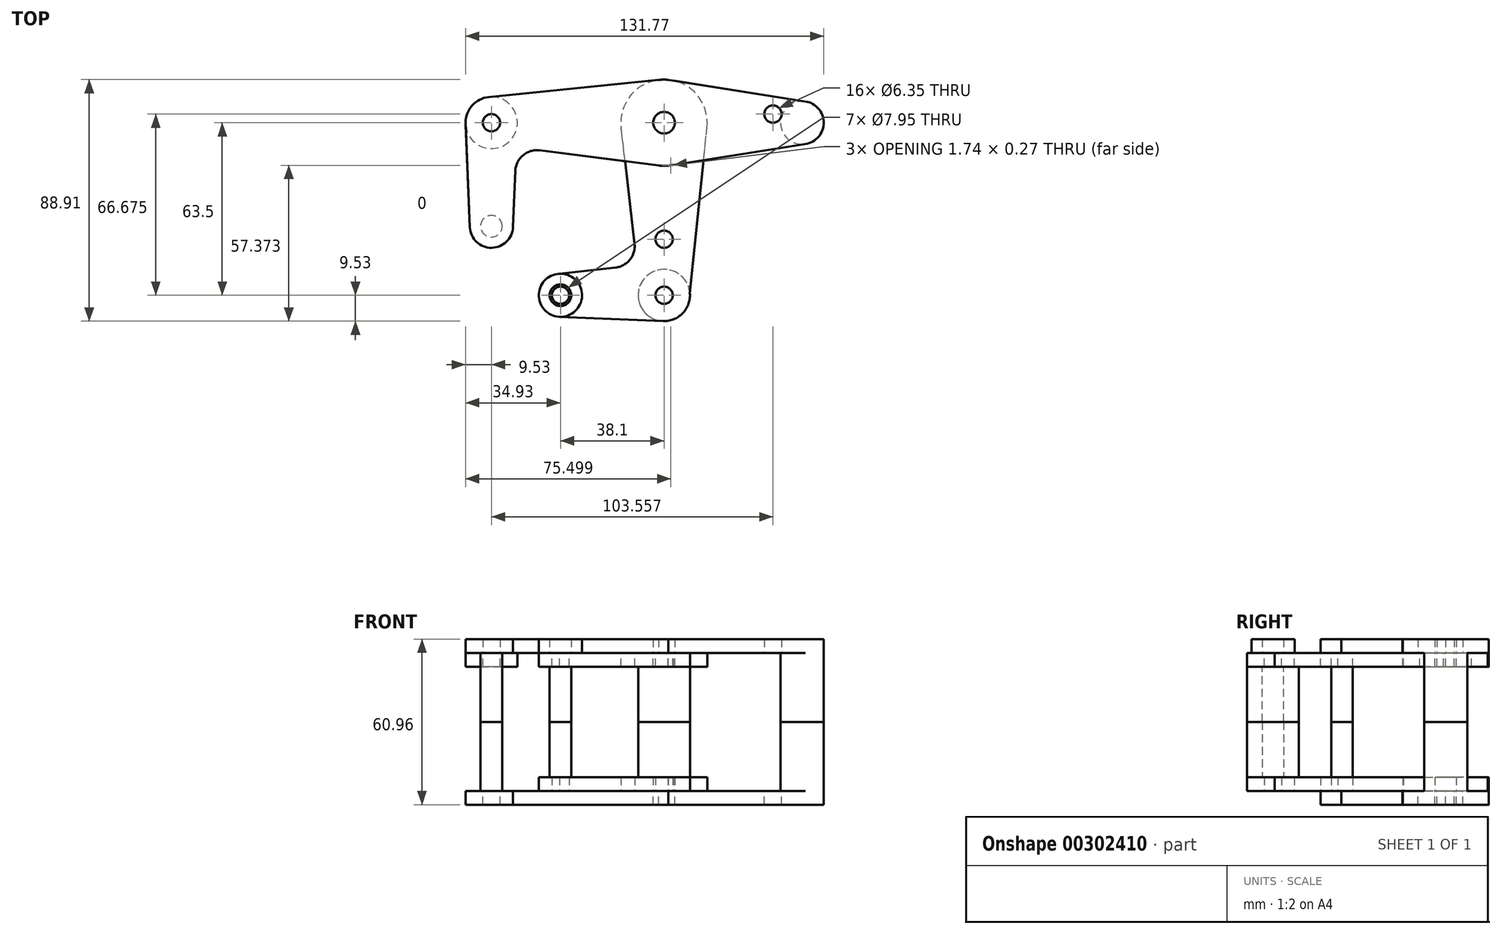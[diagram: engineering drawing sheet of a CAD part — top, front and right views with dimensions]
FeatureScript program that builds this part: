
annotation { "Feature Type Name" : "Feature", "Feature Type Description" : "" }
export const myFeature = defineFeature(function(context is Context, id is Id, definition is map)
    precondition{}
    {
        {
            var Q0;
            Q0=qCreatedBy(makeId("Top.planeOp"),FACE);
            var sketch = newSketch(context, id + "F0", { "sketchPlane" : qUnion([Q0])});
            skCircle(sketch, "E0", {"center": v(0, 0) * mm, "radius": 15.88 * mm});
            skCircle(sketch, "E1", {"center": v(0, 0) * mm, "radius": 3.98 * mm});
            skLineSegment(sketch, "E2", {"start": v(0, 0) * mm, "end": v(50.8, 0) * mm, "construction": true});
            skCircle(sketch, "E3", {"center": v(50.8, 0) * mm, "radius": 7.94 * mm});
            skCircle(sketch, "E4", {"center": v(50.8, 0) * mm, "radius": 3.18 * mm});
            skLineSegment(sketch, "E5", {"start": v(0, 0) * mm, "end": v(-63.5, 0) * mm, "construction": true});
            skCircle(sketch, "E6", {"center": v(-63.5, 0) * mm, "radius": 9.53 * mm});
            skCircle(sketch, "E7", {"center": v(-63.5, 0) * mm, "radius": 3.18 * mm});
            skLineSegment(sketch, "E8", {"start": v(-63.5, 0) * mm, "end": v(-63.5, -38.1) * mm, "construction": true});
            skCircle(sketch, "E9", {"center": v(-63.5, -38.1) * mm, "radius": 7.94 * mm});
            skCircle(sketch, "E10", {"center": v(-63.5, -38.1) * mm, "radius": 3.18 * mm});
            skLineSegment(sketch, "E11", {"start": v(0, 0) * mm, "end": v(0, -63.5) * mm, "construction": true});
            skCircle(sketch, "E12", {"center": v(0, -63.5) * mm, "radius": 9.53 * mm});
            skCircle(sketch, "E13", {"center": v(0, -63.5) * mm, "radius": 3.18 * mm});
            skLineSegment(sketch, "E14", {"start": v(0, -63.5) * mm, "end": v(-38.1, -63.5) * mm, "construction": true});
            skCircle(sketch, "E15", {"center": v(-38.1, -63.5) * mm, "radius": 7.94 * mm});
            skCircle(sketch, "E16", {"center": v(-38.1, -63.5) * mm, "radius": 3.18 * mm});
            skCircle(sketch, "E17", {"center": v(0, -42.85) * mm, "radius": 3.18 * mm});
            skLineSegment(sketch, "E18", {"start": v(-55.57, -38.32) * mm, "end": v(-54.7, -17.73) * mm});
            skLineSegment(sketch, "E19", {"start": v(-45.76, -10.17) * mm, "end": v(-2, -15.75) * mm});
            skPoint(sketch, "E20.visualSharp", {"position": v(-54.35, -9.08) * mm});
            skArc(sketch, "E20.filletArc", {"start": v(-45.76, -10.17) * mm, "mid": v(-51.9, -11.98) * mm, "end": v(-54.7, -17.73) * mm});
            skLineSegment(sketch, "E21", {"start": v(-38.48, -55.57) * mm, "end": v(-17.9, -53.31) * mm});
            skLineSegment(sketch, "E22", {"start": v(-10.86, -44.5) * mm, "end": v(-15.77, -1.81) * mm});
            skPoint(sketch, "E23.visualSharp", {"position": v(-9.95, -52.44) * mm});
            skArc(sketch, "E23.filletArc", {"start": v(-17.9, -53.31) * mm, "mid": v(-12.54, -50.37) * mm, "end": v(-10.86, -44.5) * mm});
            skLineSegment(sketch, "E24", {"start": v(-38.49, -71.43) * mm, "end": v(0, -73.03) * mm});
            skLineSegment(sketch, "E25", {"start": v(9.5, -62.84) * mm, "end": v(15.8, -1.62) * mm});
            skLineSegment(sketch, "E26", {"start": v(1.6, -15.8) * mm, "end": v(52.04, -7.84) * mm});
            skLineSegment(sketch, "E27", {"start": v(1.46, 15.8) * mm, "end": v(52.04, 7.84) * mm});
            skLineSegment(sketch, "E28", {"start": v(-1.98, 15.75) * mm, "end": v(-64.45, 9.48) * mm});
            skLineSegment(sketch, "E29", {"start": v(-73.03, 0) * mm, "end": v(-71.43, -38.43) * mm});
            skCircle(sketch, "E30", {"center": v(40.06, 3.18) * mm, "radius": 3.18 * mm});
            skCircle(sketch, "E31", {"center": v(-63.5, -38.1) * mm, "radius": 3.98 * mm});
            skCircle(sketch, "E32", {"center": v(-38.1, -63.5) * mm, "radius": 3.98 * mm});
            skSolve(sketch);
        }
        {
            var Q0;
            {var subQ0=sQuery(id+"F0.wireOp",EDGE,"E27");var subQ1=sQuery(id+"F0.wireOp",EDGE,"E0");var subQ2=makeQuery(id+"F0.imprint","INTERSECT",VERTEX,{"disambiguationData":[OD(0.0)],"derivedFrom":[subQ1,subQ0]});Q0=makeQuery(id+"F0.imprint","IMPRINT",FACE,{"disambiguationData":[TD([[makeQuery(id+"F0.imprint","IMPRINT",EDGE,{"disambiguationData":[TD([[subQ2,1.0]])],"derivedFrom":subQ1}),1.0]])]});}
            var Q1;
            {var subQ0=sQuery(id+"F0.wireOp",EDGE,"E29");var subQ1=sQuery(id+"F0.wireOp",EDGE,"E6");var subQ2=makeQuery(id+"F0.imprint","INTERSECT",VERTEX,{"disambiguationData":[OD(0.0)],"derivedFrom":[subQ1,subQ0]});Q1=makeQuery(id+"F0.imprint","IMPRINT",FACE,{"disambiguationData":[TD([[makeQuery(id+"F0.imprint","IMPRINT",EDGE,{"disambiguationData":[TD([[subQ2,-1.0]])],"derivedFrom":subQ1}),1.0]])]});}
            var Q2;
            {var subQ0=sQuery(id+"F0.wireOp",EDGE,"E24");var subQ1=sQuery(id+"F0.wireOp",EDGE,"E15");var subQ2=makeQuery(id+"F0.imprint","INTERSECT",VERTEX,{"disambiguationData":[OD(0.0)],"derivedFrom":[subQ1,subQ0]});Q2=makeQuery(id+"F0.imprint","IMPRINT",FACE,{"disambiguationData":[TD([[makeQuery(id+"F0.imprint","IMPRINT",EDGE,{"disambiguationData":[TD([[subQ2,-1.0]])],"derivedFrom":subQ1}),1.0]])]});}
            var Q3;
            Q3=makeQuery(id+"F0.imprint","IMPRINT",FACE,{"disambiguationData":[TD([[makeQuery(id+"F0.imprint","IMPRINT",EDGE,{"derivedFrom":sQuery(id+"F0.wireOp",EDGE,"E4")}),-1.0]])]});
            var Q4;
            Q4=makeQuery(id+"F0.imprint","IMPRINT",FACE,{"disambiguationData":[TD([[makeQuery(id+"F0.imprint","IMPRINT",EDGE,{"derivedFrom":sQuery(id+"F0.wireOp",EDGE,"E10")}),-1.0]])]});
            var Q5;
            {var subQ0=sQuery(id+"F0.wireOp",EDGE,"E19");var subQ1=sQuery(id+"F0.wireOp",EDGE,"E0");var subQ2=makeQuery(id+"F0.imprint","INTERSECT",VERTEX,{"derivedFrom":[subQ1,subQ0]});Q5=makeQuery(id+"F0.imprint","IMPRINT",FACE,{"disambiguationData":[TD([[makeQuery(id+"F0.imprint","IMPRINT",EDGE,{"disambiguationData":[TD([[subQ2,1.0]])],"derivedFrom":subQ1}),-1.0]])]});}
            var Q6;
            {var subQ0=sQuery(id+"F0.wireOp",EDGE,"E25");var subQ1=sQuery(id+"F0.wireOp",EDGE,"E0");var subQ2=makeQuery(id+"F0.imprint","INTERSECT",VERTEX,{"derivedFrom":[subQ1,subQ0]});Q6=makeQuery(id+"F0.imprint","IMPRINT",FACE,{"disambiguationData":[TD([[makeQuery(id+"F0.imprint","IMPRINT",EDGE,{"disambiguationData":[TD([[subQ2,1.0]])],"derivedFrom":subQ1}),-1.0]])]});}
            var Q7;
            Q7=makeQuery(id+"F0.imprint","IMPRINT",FACE,{"disambiguationData":[TD([[makeQuery(id+"F0.imprint","IMPRINT",EDGE,{"derivedFrom":sQuery(id+"F0.wireOp",EDGE,"E7")}),-1.0]])]});
            var Q8;
            {var subQ4=sQuery(id+"F0.wireOp",EDGE,"E18");Q8=makeQuery(id+"F0.imprint","IMPRINT",FACE,{"disambiguationData":[TD([[makeQuery(id+"F0.imprint","IMPRINT",EDGE,{"derivedFrom":subQ4}),1.0]])]});}
            var Q9;
            Q9=makeQuery(id+"F0.imprint","IMPRINT",FACE,{"disambiguationData":[TD([[makeQuery(id+"F0.imprint","IMPRINT",EDGE,{"derivedFrom":sQuery(id+"F0.wireOp",EDGE,"E30")}),-1.0]])]});
            var Q10;
            Q10=makeQuery(id+"F0.imprint","IMPRINT",FACE,{"disambiguationData":[TD([[makeQuery(id+"F0.imprint","IMPRINT",EDGE,{"derivedFrom":sQuery(id+"F0.wireOp",EDGE,"E1")}),-1.0]])]});
            var Q11;
            Q11=makeQuery(id+"F0.imprint","IMPRINT",FACE,{"disambiguationData":[TD([[makeQuery(id+"F0.imprint","IMPRINT",EDGE,{"derivedFrom":sQuery(id+"F0.wireOp",EDGE,"E31")}),-1.0]])]});
            extrude(context, id + "F1", {"entities" : qUnion([Q0, Q1, Q2, Q3, Q4, Q5, Q6, Q7, Q8, Q9, Q10, Q11]), "depth" : 5.08 * mm});
        }
        {
            var Q0;
            {var subQ0=sQuery(id+"F0.wireOp",EDGE,"E27");var subQ1=sQuery(id+"F0.wireOp",EDGE,"E0");var subQ2=makeQuery(id+"F0.imprint","INTERSECT",VERTEX,{"disambiguationData":[OD(0.0)],"derivedFrom":[subQ1,subQ0]});Q0=makeQuery(id+"F0.imprint","IMPRINT",FACE,{"disambiguationData":[TD([[makeQuery(id+"F0.imprint","IMPRINT",EDGE,{"disambiguationData":[TD([[subQ2,1.0]])],"derivedFrom":subQ1}),1.0]])]});}
            var Q1;
            {var subQ0=sQuery(id+"F0.wireOp",EDGE,"E29");var subQ1=sQuery(id+"F0.wireOp",EDGE,"E6");var subQ2=makeQuery(id+"F0.imprint","INTERSECT",VERTEX,{"disambiguationData":[OD(0.0)],"derivedFrom":[subQ1,subQ0]});Q1=makeQuery(id+"F0.imprint","IMPRINT",FACE,{"disambiguationData":[TD([[makeQuery(id+"F0.imprint","IMPRINT",EDGE,{"disambiguationData":[TD([[subQ2,-1.0]])],"derivedFrom":subQ1}),1.0]])]});}
            var Q2;
            {var subQ0=sQuery(id+"F0.wireOp",EDGE,"E24");var subQ1=sQuery(id+"F0.wireOp",EDGE,"E15");var subQ2=makeQuery(id+"F0.imprint","INTERSECT",VERTEX,{"disambiguationData":[OD(0.0)],"derivedFrom":[subQ1,subQ0]});Q2=makeQuery(id+"F0.imprint","IMPRINT",FACE,{"disambiguationData":[TD([[makeQuery(id+"F0.imprint","IMPRINT",EDGE,{"disambiguationData":[TD([[subQ2,-1.0]])],"derivedFrom":subQ1}),1.0]])]});}
            var Q3;
            Q3=makeQuery(id+"F0.imprint","IMPRINT",FACE,{"disambiguationData":[TD([[makeQuery(id+"F0.imprint","IMPRINT",EDGE,{"derivedFrom":sQuery(id+"F0.wireOp",EDGE,"E13")}),-1.0]])]});
            var Q4;
            {var subQ0=sQuery(id+"F0.wireOp",EDGE,"E19");var subQ1=sQuery(id+"F0.wireOp",EDGE,"E0");var subQ2=makeQuery(id+"F0.imprint","INTERSECT",VERTEX,{"derivedFrom":[subQ1,subQ0]});Q4=makeQuery(id+"F0.imprint","IMPRINT",FACE,{"disambiguationData":[TD([[makeQuery(id+"F0.imprint","IMPRINT",EDGE,{"disambiguationData":[TD([[subQ2,1.0]])],"derivedFrom":subQ1}),-1.0]])]});}
            var Q5;
            {var subQ0=sQuery(id+"F0.wireOp",EDGE,"E25");var subQ1=sQuery(id+"F0.wireOp",EDGE,"E0");var subQ2=makeQuery(id+"F0.imprint","INTERSECT",VERTEX,{"derivedFrom":[subQ1,subQ0]});Q5=makeQuery(id+"F0.imprint","IMPRINT",FACE,{"disambiguationData":[TD([[makeQuery(id+"F0.imprint","IMPRINT",EDGE,{"disambiguationData":[TD([[subQ2,1.0]])],"derivedFrom":subQ1}),-1.0]])]});}
            var Q6;
            Q6=makeQuery(id+"F0.imprint","IMPRINT",FACE,{"disambiguationData":[TD([[makeQuery(id+"F0.imprint","IMPRINT",EDGE,{"derivedFrom":sQuery(id+"F0.wireOp",EDGE,"E17")}),-1.0]])]});
            var Q7;
            Q7=makeQuery(id+"F0.imprint","IMPRINT",FACE,{"disambiguationData":[TD([[makeQuery(id+"F0.imprint","IMPRINT",EDGE,{"derivedFrom":sQuery(id+"F0.wireOp",EDGE,"E1")}),-1.0]])]});
            var Q8;
            Q8=makeQuery(id+"F0.imprint","IMPRINT",FACE,{"disambiguationData":[TD([[makeQuery(id+"F0.imprint","IMPRINT",EDGE,{"derivedFrom":sQuery(id+"F0.wireOp",EDGE,"E16")}),-1.0]])]});
            var Q9;
            Q9=makeQuery(id+"F0.imprint","IMPRINT",FACE,{"disambiguationData":[TD([[makeQuery(id+"F0.imprint","IMPRINT",EDGE,{"derivedFrom":sQuery(id+"F0.wireOp",EDGE,"E32")}),-1.0]])]});
            extrude(context, id + "F2", {"entities" : qUnion([Q0, Q1, Q2, Q3, Q4, Q5, Q6, Q7, Q8, Q9]), "oppositeDirection" : true, "depth" : 5.08 * mm});
        }
        {
            var Q0;
            Q0=qCreatedBy(makeId("Top.planeOp"),FACE);
            cPlane(context, id + "F3", {"entities" : qUnion([Q0]), "cplaneType" : CPlaneType.OFFSET, "offset" : 25.4 * mm, "oppositeDirection" : true, "width" : 152.4 * mm, "height" : 152.4 * mm});
        }
        {
            var Q0;
            Q0=makeQuery(id+"F0.imprint","IMPRINT",FACE,{"disambiguationData":[TD([[makeQuery(id+"F0.imprint","IMPRINT",EDGE,{"derivedFrom":sQuery(id+"F0.wireOp",EDGE,"E10")}),-1.0]])]});
            var Q1;
            Q1=makeQuery(id+"F0.imprint","IMPRINT",FACE,{"disambiguationData":[TD([[makeQuery(id+"F0.imprint","IMPRINT",EDGE,{"derivedFrom":sQuery(id+"F0.wireOp",EDGE,"E4")}),-1.0]])]});
            var Q2;
            Q2=makeQuery(id+"F0.imprint","IMPRINT",FACE,{"disambiguationData":[TD([[makeQuery(id+"F0.imprint","IMPRINT",EDGE,{"derivedFrom":sQuery(id+"F0.wireOp",EDGE,"E16")}),-1.0]])]});
            var Q3;
            Q3=makeQuery(id+"F0.imprint","IMPRINT",FACE,{"disambiguationData":[TD([[makeQuery(id+"F0.imprint","IMPRINT",EDGE,{"derivedFrom":sQuery(id+"F0.wireOp",EDGE,"E13")}),-1.0]])]});
            var Q4;
            Q4=makeQuery(id+"F0.imprint","IMPRINT",FACE,{"disambiguationData":[TD([[makeQuery(id+"F0.imprint","IMPRINT",EDGE,{"derivedFrom":sQuery(id+"F0.wireOp",EDGE,"E10")}),1.0]])]});
            var Q5;
            Q5=makeQuery(id+"F0.imprint","IMPRINT",FACE,{"disambiguationData":[TD([[makeQuery(id+"F0.imprint","IMPRINT",EDGE,{"derivedFrom":sQuery(id+"F0.wireOp",EDGE,"E16")}),1.0]])]});
            var Q6;
            Q6=makeQuery(id+"F0.imprint","IMPRINT",FACE,{"disambiguationData":[TD([[makeQuery(id+"F0.imprint","IMPRINT",EDGE,{"derivedFrom":sQuery(id+"F0.wireOp",EDGE,"E13")}),1.0]])]});
            var Q7;
            Q7=makeQuery(id+"F0.imprint","IMPRINT",FACE,{"disambiguationData":[TD([[makeQuery(id+"F0.imprint","IMPRINT",EDGE,{"derivedFrom":sQuery(id+"F0.wireOp",EDGE,"E4")}),1.0]])]});
            var Q8;
            Q8=qCreatedBy(id+"F3.planeOp",FACE);
            extrude(context, id + "F4", {"entities" : qUnion([Q0, Q1, Q2, Q3, Q4, Q5, Q6, Q7]), "endBound" : BoundingType.UP_TO_SURFACE, "oppositeDirection" : true, "endBoundEntityFace" : qUnion([Q8]), "depth" : 25.4 * mm});
        }
        {
            var Q0;
            Q0=makeQuery(id+"F0.imprint","IMPRINT",FACE,{"disambiguationData":[TD([[makeQuery(id+"F0.imprint","IMPRINT",EDGE,{"derivedFrom":sQuery(id+"F0.wireOp",EDGE,"E4")}),1.0]])]});
            extrude(context, id + "F5", {"entities" : qUnion([Q0]), "operationType" : NewBodyOperationType.ADD, "depth" : 5.08 * mm});
        }
        {
            var Q0;
            Q0=makeQuery(id+"F0.imprint","IMPRINT",FACE,{"disambiguationData":[TD([[makeQuery(id+"F0.imprint","IMPRINT",EDGE,{"derivedFrom":sQuery(id+"F0.wireOp",EDGE,"E10")}),1.0]])]});
            extrude(context, id + "F6", {"entities" : qUnion([Q0]), "operationType" : NewBodyOperationType.ADD, "depth" : 5.08 * mm});
        }
        {
            var Q0;
            Q0=makeQuery(id+"F1.opExtrude","SWEPT_BODY",BODY,{"disambiguationData":[OSD([sQuery(id+"F0.wireOp",EDGE,"E0"),sQuery(id+"F0.wireOp",EDGE,"E1"),sQuery(id+"F0.wireOp",EDGE,"E3"),sQuery(id+"F0.wireOp",EDGE,"E4"),sQuery(id+"F0.wireOp",EDGE,"E6"),sQuery(id+"F0.wireOp",EDGE,"E7"),sQuery(id+"F0.wireOp",EDGE,"E9"),sQuery(id+"F0.wireOp",EDGE,"E10"),sQuery(id+"F0.wireOp",EDGE,"E18"),sQuery(id+"F0.wireOp",EDGE,"E19"),sQuery(id+"F0.wireOp",EDGE,"E20.filletArc"),sQuery(id+"F0.wireOp",EDGE,"E26"),sQuery(id+"F0.wireOp",EDGE,"E27"),sQuery(id+"F0.wireOp",EDGE,"E28"),sQuery(id+"F0.wireOp",EDGE,"E29"),sQuery(id+"F0.wireOp",EDGE,"E30")])]});
            var Q1;
            Q1=makeQuery(id+"F2.opExtrude","SWEPT_BODY",BODY,{"disambiguationData":[OSD([sQuery(id+"F0.wireOp",EDGE,"E0"),sQuery(id+"F0.wireOp",EDGE,"E1"),sQuery(id+"F0.wireOp",EDGE,"E12"),sQuery(id+"F0.wireOp",EDGE,"E13"),sQuery(id+"F0.wireOp",EDGE,"E15"),sQuery(id+"F0.wireOp",EDGE,"E16"),sQuery(id+"F0.wireOp",EDGE,"E17"),sQuery(id+"F0.wireOp",EDGE,"E21"),sQuery(id+"F0.wireOp",EDGE,"E22"),sQuery(id+"F0.wireOp",EDGE,"E23.filletArc"),sQuery(id+"F0.wireOp",EDGE,"E24"),sQuery(id+"F0.wireOp",EDGE,"E25"),sQuery(id+"F0.wireOp",EDGE,"E26")])]});
            var Q2;
            Q2=makeQuery(id+"F4.opExtrude","SWEPT_BODY",BODY,{"disambiguationData":[OSD([sQuery(id+"F0.wireOp",EDGE,"E3")])]});
            var Q3;
            Q3=makeQuery(id+"F4.opExtrude","SWEPT_BODY",BODY,{"disambiguationData":[OSD([sQuery(id+"F0.wireOp",EDGE,"E12")])]});
            var Q4;
            Q4=makeQuery(id+"F4.opExtrude","SWEPT_BODY",BODY,{"disambiguationData":[OSD([sQuery(id+"F0.wireOp",EDGE,"E31")])]});
            var Q5;
            Q5=makeQuery(id+"F4.opExtrude","SWEPT_BODY",BODY,{"disambiguationData":[OSD([sQuery(id+"F0.wireOp",EDGE,"E32")])]});
            var Q6;
            Q6=qCreatedBy(id+"F3.planeOp",FACE);
            mirror(context, id + "F7", {"entities" : qUnion([Q0, Q1, Q2, Q3, Q4, Q5]), "mirrorPlane" : qUnion([Q6])});
        }
        {
            var Q0;
            Q0=makeQuery(id+"F2.opExtrude","SWEPT_BODY",BODY,{"disambiguationData":[OSD([sQuery(id+"F0.wireOp",EDGE,"E0"),sQuery(id+"F0.wireOp",EDGE,"E1"),sQuery(id+"F0.wireOp",EDGE,"E12"),sQuery(id+"F0.wireOp",EDGE,"E13"),sQuery(id+"F0.wireOp",EDGE,"E15"),sQuery(id+"F0.wireOp",EDGE,"E16"),sQuery(id+"F0.wireOp",EDGE,"E17"),sQuery(id+"F0.wireOp",EDGE,"E21"),sQuery(id+"F0.wireOp",EDGE,"E22"),sQuery(id+"F0.wireOp",EDGE,"E23.filletArc"),sQuery(id+"F0.wireOp",EDGE,"E24"),sQuery(id+"F0.wireOp",EDGE,"E25"),sQuery(id+"F0.wireOp",EDGE,"E26")])]});
            var Q1;
            Q1=makeQuery(id+"F4.opExtrude","SWEPT_BODY",BODY,{"disambiguationData":[OSD([sQuery(id+"F0.wireOp",EDGE,"E12")])]});
            booleanBodies(context, id + "F8", {"operationType" : BooleanOperationType.SUBTRACTION, "tools" : qUnion([Q0]), "targets" : qUnion([Q1]), "keepTools" : true});
        }
        {
            var Q0;
            Q0=makeQuery(id+"F2.opExtrude","SWEPT_BODY",BODY,{"disambiguationData":[OSD([sQuery(id+"F0.wireOp",EDGE,"E0"),sQuery(id+"F0.wireOp",EDGE,"E1"),sQuery(id+"F0.wireOp",EDGE,"E12"),sQuery(id+"F0.wireOp",EDGE,"E13"),sQuery(id+"F0.wireOp",EDGE,"E15"),sQuery(id+"F0.wireOp",EDGE,"E16"),sQuery(id+"F0.wireOp",EDGE,"E17"),sQuery(id+"F0.wireOp",EDGE,"E21"),sQuery(id+"F0.wireOp",EDGE,"E22"),sQuery(id+"F0.wireOp",EDGE,"E23.filletArc"),sQuery(id+"F0.wireOp",EDGE,"E24"),sQuery(id+"F0.wireOp",EDGE,"E25"),sQuery(id+"F0.wireOp",EDGE,"E26")])]});
            var Q1;
            Q1=makeQuery(id+"F4.opExtrude","SWEPT_BODY",BODY,{"disambiguationData":[OSD([sQuery(id+"F0.wireOp",EDGE,"E32")])]});
            booleanBodies(context, id + "F9", {"operationType" : BooleanOperationType.SUBTRACTION, "tools" : qUnion([Q0]), "targets" : qUnion([Q1]), "keepTools" : true});
        }
        {
            var Q0;
            Q0=makeQuery(id+"F7.opPattern","COPY",BODY,{"derivedFrom":makeQuery(id+"F2.opExtrude","SWEPT_BODY",BODY,{"disambiguationData":[OSD([sQuery(id+"F0.wireOp",EDGE,"E0"),sQuery(id+"F0.wireOp",EDGE,"E1"),sQuery(id+"F0.wireOp",EDGE,"E12"),sQuery(id+"F0.wireOp",EDGE,"E13"),sQuery(id+"F0.wireOp",EDGE,"E15"),sQuery(id+"F0.wireOp",EDGE,"E16"),sQuery(id+"F0.wireOp",EDGE,"E17"),sQuery(id+"F0.wireOp",EDGE,"E21"),sQuery(id+"F0.wireOp",EDGE,"E22"),sQuery(id+"F0.wireOp",EDGE,"E23.filletArc"),sQuery(id+"F0.wireOp",EDGE,"E24"),sQuery(id+"F0.wireOp",EDGE,"E25"),sQuery(id+"F0.wireOp",EDGE,"E26")])]}),"instanceName":"1"});
            var Q1;
            Q1=makeQuery(id+"F7.opPattern","COPY",BODY,{"derivedFrom":makeQuery(id+"F4.opExtrude","SWEPT_BODY",BODY,{"disambiguationData":[OSD([sQuery(id+"F0.wireOp",EDGE,"E12")])]}),"instanceName":"1"});
            var Q2;
            Q2=makeQuery(id+"F7.opPattern","COPY",BODY,{"derivedFrom":makeQuery(id+"F4.opExtrude","SWEPT_BODY",BODY,{"disambiguationData":[OSD([sQuery(id+"F0.wireOp",EDGE,"E32")])]}),"instanceName":"1"});
            booleanBodies(context, id + "F10", {"operationType" : BooleanOperationType.SUBTRACTION, "tools" : qUnion([Q0]), "targets" : qUnion([Q1, Q2]), "keepTools" : true});
        }
        {
            var Q0;
            Q0=makeQuery(id+"F1.opExtrude","SWEPT_BODY",BODY,{"disambiguationData":[OSD([sQuery(id+"F0.wireOp",EDGE,"E0"),sQuery(id+"F0.wireOp",EDGE,"E1"),sQuery(id+"F0.wireOp",EDGE,"E3"),sQuery(id+"F0.wireOp",EDGE,"E4"),sQuery(id+"F0.wireOp",EDGE,"E6"),sQuery(id+"F0.wireOp",EDGE,"E7"),sQuery(id+"F0.wireOp",EDGE,"E9"),sQuery(id+"F0.wireOp",EDGE,"E10"),sQuery(id+"F0.wireOp",EDGE,"E18"),sQuery(id+"F0.wireOp",EDGE,"E19"),sQuery(id+"F0.wireOp",EDGE,"E20.filletArc"),sQuery(id+"F0.wireOp",EDGE,"E26"),sQuery(id+"F0.wireOp",EDGE,"E27"),sQuery(id+"F0.wireOp",EDGE,"E28"),sQuery(id+"F0.wireOp",EDGE,"E29"),sQuery(id+"F0.wireOp",EDGE,"E30")])]});
            var Q1;
            Q1=makeQuery(id+"F2.opExtrude","SWEPT_BODY",BODY,{"disambiguationData":[OSD([sQuery(id+"F0.wireOp",EDGE,"E0"),sQuery(id+"F0.wireOp",EDGE,"E1"),sQuery(id+"F0.wireOp",EDGE,"E12"),sQuery(id+"F0.wireOp",EDGE,"E13"),sQuery(id+"F0.wireOp",EDGE,"E15"),sQuery(id+"F0.wireOp",EDGE,"E16"),sQuery(id+"F0.wireOp",EDGE,"E17"),sQuery(id+"F0.wireOp",EDGE,"E21"),sQuery(id+"F0.wireOp",EDGE,"E22"),sQuery(id+"F0.wireOp",EDGE,"E23.filletArc"),sQuery(id+"F0.wireOp",EDGE,"E24"),sQuery(id+"F0.wireOp",EDGE,"E25"),sQuery(id+"F0.wireOp",EDGE,"E26")])]});
            var Q2;
            Q2=qCreatedBy(id+"F3.planeOp",FACE);
            mirror(context, id + "F11", {"entities" : qUnion([Q0, Q1]), "mirrorPlane" : qUnion([Q2])});
        }
    });
